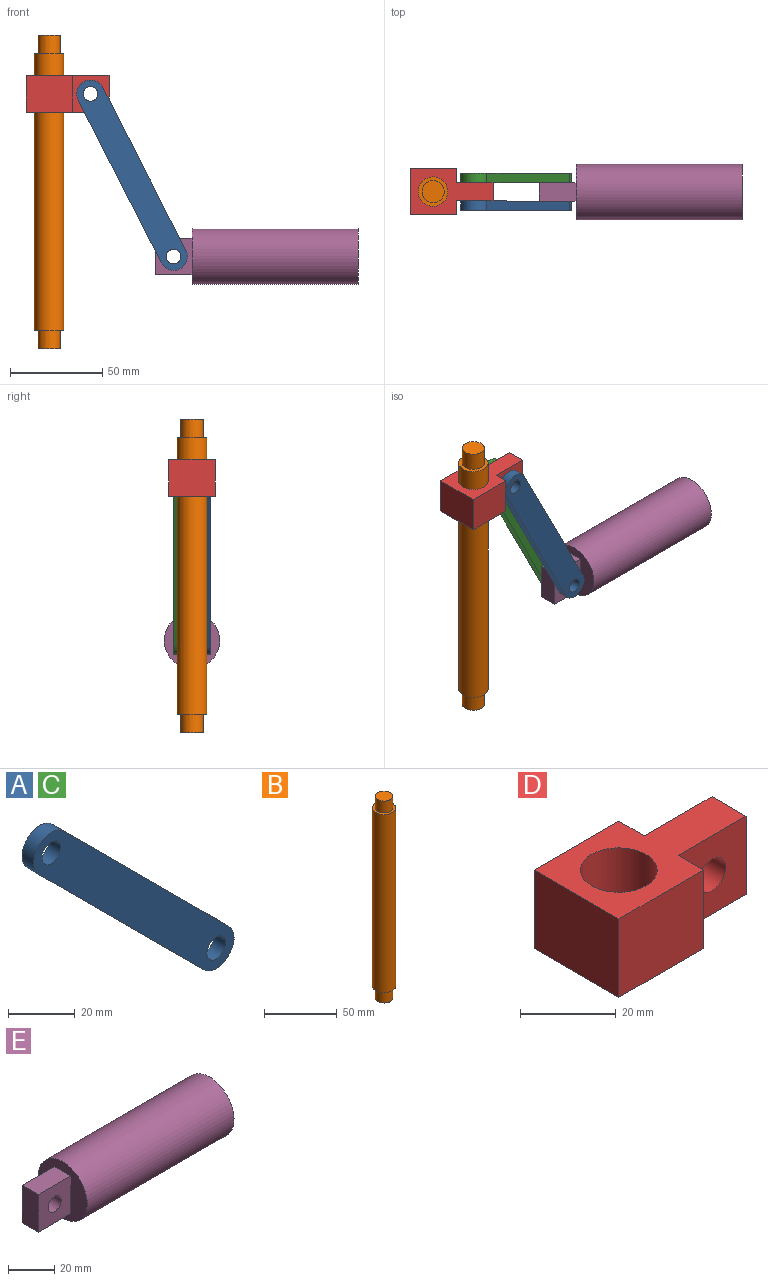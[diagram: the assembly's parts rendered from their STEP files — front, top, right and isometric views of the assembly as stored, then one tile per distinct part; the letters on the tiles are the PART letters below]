
ASSEMBLY  parts=5 mates=6
PART A: 8 faces, bbox 85x5x85 mm
  f0: plane 70x70mm, normal (-0.71,0,-0.71), area 495mm2, adj f1,f4,f6,f7
  f1: cylinder r=7.5mm len=12.8mm, axis (0,1,0), area 117.8mm2, adj f0,f2,f6,f7
  f2: plane 70x70mm, normal (0.71,0,0.71), area 495mm2, adj f1,f4,f6,f7
  f3: cylinder r=4mm len=8mm, axis (0,1,0), area 125.7mm2, adj f6,f7
  f4: cylinder r=7.5mm len=12.8mm, axis (0,1,0), area 117.8mm2, adj f0,f2,f6,f7
  f5: cylinder r=4mm len=8mm, axis (0,1,0), area 125.7mm2, adj f6,f7
  f6: plane 85x85mm, normal (0,-1,0), area 1561.1mm2, adj f0,f1,f2,f3,f4,f5
  f7: plane 85x85mm, normal (0,1,0), area 1561.1mm2, adj f0,f1,f2,f3,f4,f5
PART B: 7 faces, bbox 16x16x170 mm
  f0: plane 12x12mm, normal (0,0,1), area 113.1mm2, adj f1
  f1: cylinder r=6mm len=12mm, axis (0,0,1), area 377mm2, adj f0,f2
  f2: plane 16x16mm, normal (0,0,1), area 88mm2, adj f1,f3
  f3: cylinder r=8mm len=150mm, axis (0,0,1), area 7539.8mm2, adj f2,f4
  f4: plane 16x16mm, normal (0,0,-1), area 88mm2, adj f3,f5
  f5: cylinder r=6mm len=12mm, axis (0,0,1), area 377mm2, adj f4,f6
  f6: plane 12x12mm, normal (0,0,-1), area 113.1mm2, adj f5
PART C: same geometry as A
PART D: 12 faces, bbox 45x25x20 mm
  f0: plane 20x7.5mm, normal (1,0,0), area 150mm2, adj f1,f3,f6,f10
  f1: plane 45x25mm, normal (0,0,1), area 623.9mm2, adj f0,f2,f4,f5,f6,f8,f9,f10
  f2: plane 25x20mm, normal (-1,0,0), area 500mm2, adj f1,f3,f5,f6
  f3: plane 45x25mm, normal (0,0,-1), area 623.9mm2, adj f0,f2,f4,f5,f6,f8,f9,f10
  f4: plane 20x7.5mm, normal (1,0,0), area 150mm2, adj f1,f3,f5,f9
  f5: plane 25x20mm, normal (0,-1,0), area 500mm2, adj f1,f2,f3,f4
  f6: plane 25x20mm, normal (0,1,0), area 500mm2, adj f0,f1,f2,f3
  f7: cylinder r=4mm len=10mm, axis (0,1,0), area 251.3mm2, adj f9,f10
  f8: plane 20x10mm, normal (1,0,0), area 200mm2, adj f1,f3,f9,f10
  f9: plane 20x20mm, normal (0,-1,0), area 349.7mm2, adj f1,f3,f4,f7,f8
  f10: plane 20x20mm, normal (0,1,0), area 349.7mm2, adj f0,f1,f3,f7,f8
  f11: cylinder r=8mm len=20mm, axis (0,0,1), area 1005.3mm2, adj f1,f3
PART E: 9 faces, bbox 110x30x30 mm
  f0: plane 30x30mm, normal (-1,0,0), area 506.9mm2, adj f2,f3,f6,f7,f8
  f1: plane 30x30mm, normal (1,0,0), area 706.9mm2, adj f2
  f2: cylinder r=15mm len=90mm, axis (1,0,0), area 8482.3mm2, adj f0,f1
  f3: plane 20x10mm, normal (0,0,1), area 200mm2, adj f0,f4,f7,f8
  f4: plane 20x10mm, normal (-1,0,0), area 200mm2, adj f3,f6,f7,f8
  f5: cylinder r=4mm len=10mm, axis (0,1,0), area 251.3mm2, adj f7,f8
  f6: plane 20x10mm, normal (0,0,-1), area 200mm2, adj f0,f4,f7,f8
  f7: plane 20x20mm, normal (0,-1,0), area 349.7mm2, adj f0,f3,f4,f5,f6
  f8: plane 20x20mm, normal (0,1,0), area 349.7mm2, adj f0,f3,f4,f5,f6
PLACE A rot(axis=(0,1,0),18deg) t=(-29.84,-5.17,49.99)mm
PLACE B t=(-0.09,-5.17,0)mm fixed
PLACE C rot(axis=(0,1,0),18deg) t=(-29.84,9.83,49.99)mm
PLACE D t=(-0.09,-5.17,38.18)mm
PLACE E t=(-25.09,-5.17,20)mm
MATE revolute A.f3 <-> D.f7  axis (0,1,0) through (22.41,-10.17,138.18)mm
MATE planar E.f6 <-> B.f1  axis (0,0,-1) through (67.41,-5.17,40)mm
MATE revolute C.f3 <-> D.f7  axis (0,-1,0) through (22.41,-0.17,138.18)mm
MATE revolute E.f5 <-> A.f1  axis (0,-1,0) through (67.41,-10.17,50)mm
MATE cylindrical A.f1 <-> C.f1  axis (0,-1,0) through (67.41,-15.17,50)mm
MATE slider D.f11 <-> B.f1  axis (0,0,1) through (-0.09,-5.17,148.18)mm
